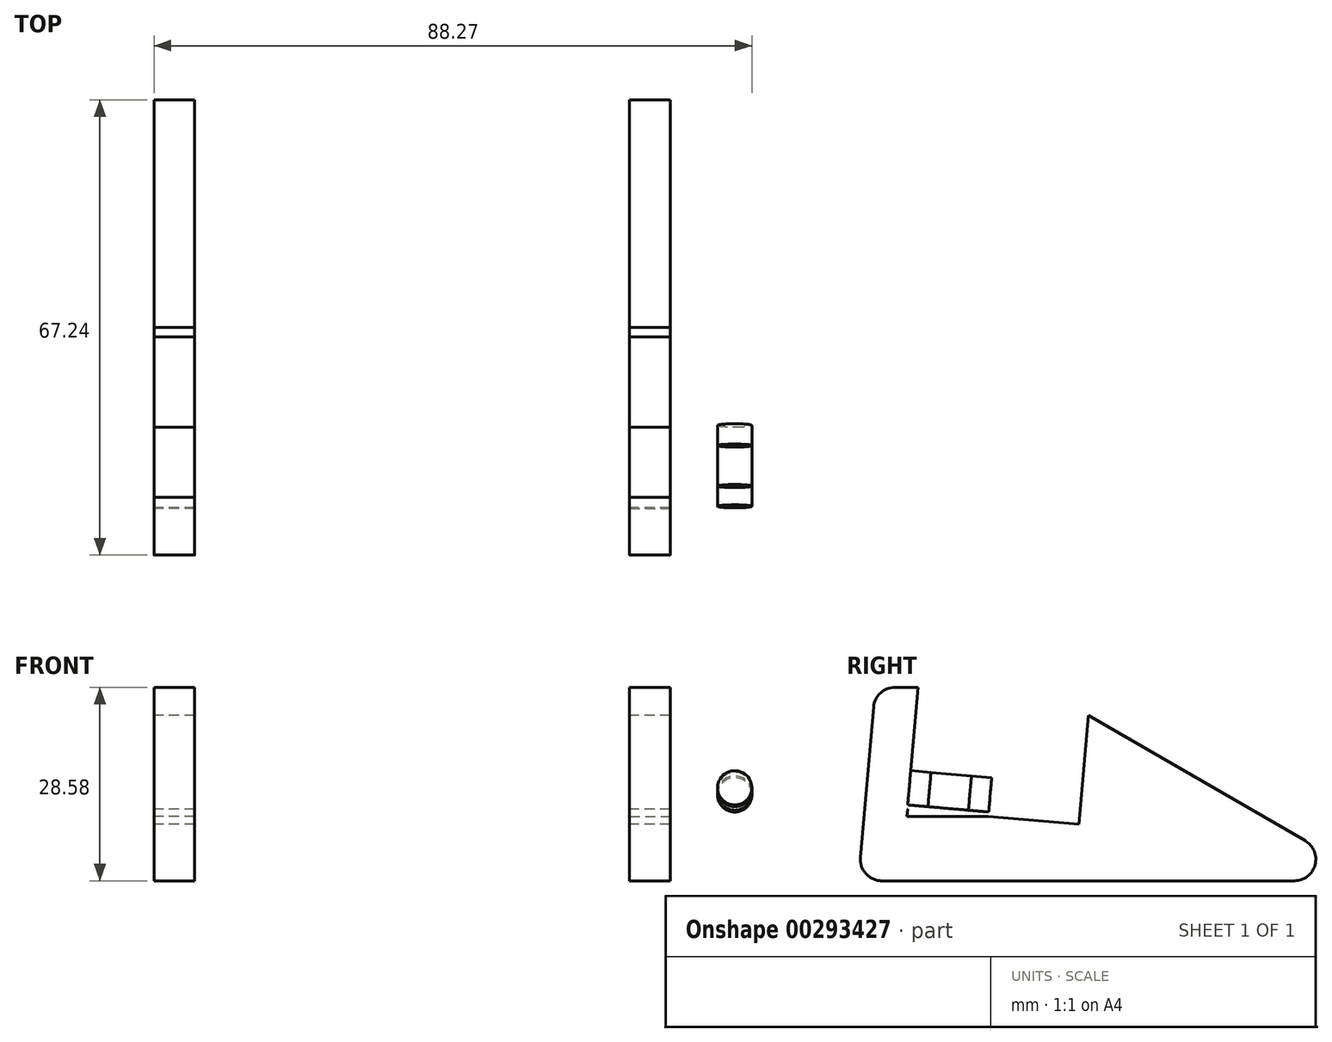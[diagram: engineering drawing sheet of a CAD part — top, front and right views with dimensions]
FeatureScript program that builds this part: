
annotation { "Feature Type Name" : "Feature", "Feature Type Description" : "" }
export const myFeature = defineFeature(function(context is Context, id is Id, definition is map)
    precondition{}
    {
        {
            var Q0;
            Q0=qCreatedBy(makeId("Right.planeOp"),FACE);
            cPlane(context, id + "F0", {"entities" : qUnion([Q0]), "cplaneType" : CPlaneType.OFFSET, "offset" : 38.1 * mm, "oppositeDirection" : true, "width" : 152.4 * mm, "height" : 152.4 * mm});
        }
        {
            var Q0;
            Q0=qCreatedBy(id+"F0.planeOp",FACE);
            var sketch = newSketch(context, id + "F1", { "sketchPlane" : qUnion([Q0])});
            skLineSegment(sketch, "E0", {"start": v(3.46, 0) * mm, "end": v(64.35, 0) * mm});
            skLineSegment(sketch, "E1", {"start": v(65.94, 5.92) * mm, "end": v(27.44, 28.15) * mm});
            skLineSegment(sketch, "E2", {"start": v(25.86, 28.57) * mm, "end": v(20.85, 28.57) * mm});
            skLineSegment(sketch, "E3", {"start": v(20.85, 28.57) * mm, "end": v(19.18, 9.53) * mm});
            skLineSegment(sketch, "E4", {"start": v(19.18, 9.52) * mm, "end": v(7.18, 9.52) * mm});
            skLineSegment(sketch, "E5", {"start": v(7.18, 9.52) * mm, "end": v(8.85, 28.57) * mm});
            skLineSegment(sketch, "E6", {"start": v(8.85, 28.57) * mm, "end": v(5.4, 28.57) * mm});
            skLineSegment(sketch, "E7", {"start": v(2.25, 25.68) * mm, "end": v(0.3, 3.45) * mm});
            skPoint(sketch, "E8.visualSharp", {"position": v(76.2, 0) * mm});
            skArc(sketch, "E8.filletArc", {"start": v(64.35, 0) * mm, "mid": v(67.42, 2.35) * mm, "end": v(65.94, 5.92) * mm});
            skPoint(sketch, "E9.visualSharp", {"position": v(0, 0) * mm});
            skArc(sketch, "E9.filletArc", {"start": v(0.3, 3.45) * mm, "mid": v(1.12, 1.03) * mm, "end": v(3.46, 0) * mm});
            skPoint(sketch, "E10.visualSharp", {"position": v(2.5, 28.57) * mm});
            skArc(sketch, "E10.filletArc", {"start": v(5.4, 28.57) * mm, "mid": v(3.26, 27.74) * mm, "end": v(2.25, 25.68) * mm});
            skPoint(sketch, "E11.visualSharp", {"position": v(26.7, 28.57) * mm});
            skArc(sketch, "E11.filletArc", {"start": v(27.44, 28.15) * mm, "mid": v(26.68, 28.47) * mm, "end": v(25.86, 28.57) * mm});
            skSolve(sketch);
        }
        {
            var Q0;
            Q0=makeQuery(id+"F1.imprint","IMPRINT",FACE,{"disambiguationData":[TD([[makeQuery(id+"F1.imprint","IMPRINT",EDGE,{"derivedFrom":sQuery(id+"F1.wireOp",EDGE,"E0")}),1.0]])]});
            extrude(context, id + "F2", {"entities" : qUnion([Q0]), "depth" : 6 * mm});
        }
        {
            var Q0;
            Q0=makeQuery(id+"F2.opExtrude","SWEPT_BODY",BODY,{"disambiguationData":[OSD([sQuery(id+"F1.wireOp",EDGE,"E0"),sQuery(id+"F1.wireOp",EDGE,"E1"),sQuery(id+"F1.wireOp",EDGE,"E2"),sQuery(id+"F1.wireOp",EDGE,"E3"),sQuery(id+"F1.wireOp",EDGE,"E4"),sQuery(id+"F1.wireOp",EDGE,"E5"),sQuery(id+"F1.wireOp",EDGE,"E6"),sQuery(id+"F1.wireOp",EDGE,"E7"),sQuery(id+"F1.wireOp",EDGE,"E8.filletArc"),sQuery(id+"F1.wireOp",EDGE,"E9.filletArc"),sQuery(id+"F1.wireOp",EDGE,"E10.filletArc"),sQuery(id+"F1.wireOp",EDGE,"E11.filletArc")])]});
            var Q1;
            Q1=qCreatedBy(makeId("Right.planeOp"),FACE);
            mirror(context, id + "F3", {"entities" : qUnion([Q0]), "mirrorPlane" : qUnion([Q1])});
        }
        {
            var Q0;
            Q0=makeQuery(id+"F2.opExtrude","SWEPT_FACE",FACE,{"disambiguationData":[OSD([sQuery(id+"F1.wireOp",EDGE,"E3")])]});
            var sketch = newSketch(context, id + "F4", { "sketchPlane" : qUnion([Q0])});
            skLineSegment(sketch, "E12.bottom", {"start": v(38.1, 11.16) * mm, "end": v(32.1, 11.16) * mm});
            skLineSegment(sketch, "E12.top", {"start": v(57.15, 214.36) * mm, "end": v(-57.15, 214.36) * mm});
            skLineSegment(sketch, "E12.left", {"start": v(57.15, 11.16) * mm, "end": v(57.15, 214.36) * mm});
            skLineSegment(sketch, "E12.right", {"start": v(-57.15, 11.16) * mm, "end": v(-57.15, 214.36) * mm});
            skPoint(sketch, "E12.middle", {"position": v(0, 112.76) * mm});
            skLineSegment(sketch, "E13", {"start": v(-57.15, 138.16) * mm, "end": v(-25.4, 214.36) * mm});
            skLineSegment(sketch, "E14", {"start": v(25.4, 214.36) * mm, "end": v(57.15, 138.16) * mm});
            skLineSegment(sketch, "E15.top", {"start": v(-57.15, 4.81) * mm, "end": v(-38.1, 4.81) * mm});
            skLineSegment(sketch, "E15.right", {"start": v(-38.1, 11.16) * mm, "end": v(-38.1, 4.81) * mm});
            skLineSegment(sketch, "E16.top", {"start": v(57.15, 4.81) * mm, "end": v(38.1, 4.81) * mm});
            skLineSegment(sketch, "E16.right", {"start": v(38.1, 11.16) * mm, "end": v(38.1, 4.81) * mm});
            skLineSegment(sketch, "E17.top", {"start": v(-32.1, 4.81) * mm, "end": v(32.1, 4.81) * mm});
            skLineSegment(sketch, "E17.left", {"start": v(-32.1, 11.16) * mm, "end": v(-32.1, 4.81) * mm});
            skLineSegment(sketch, "E17.right", {"start": v(32.1, 11.16) * mm, "end": v(32.1, 4.81) * mm});
            skLineSegment(sketch, "E18.trimOffspring", {"start": v(-32.1, 11.16) * mm, "end": v(-38.1, 11.16) * mm});
            skLineSegment(sketch, "E19", {"start": v(-57.15, 11.16) * mm, "end": v(-57.15, 4.81) * mm});
            skLineSegment(sketch, "E20", {"start": v(57.15, 11.16) * mm, "end": v(57.15, 4.81) * mm});
            skSolve(sketch);
        }
        {
            var Q0;
            Q0=makeQuery(id+"F4.imprint","IMPRINT",FACE,{"disambiguationData":[TD([[makeQuery(id+"F4.imprint","IMPRINT",EDGE,{"derivedFrom":sQuery(id+"F4.wireOp",EDGE,"E12.bottom")}),-1.0]])]});
            var Q1;
            Q1=makeQuery(id+"F4.imprint","IMPRINT",FACE,{"disambiguationData":[TD([[makeQuery(id+"F4.imprint","IMPRINT",EDGE,{"derivedFrom":sQuery(id+"F4.wireOp",EDGE,"E18.trimOffspring")}),-1.0]])]});
            extrude(context, id + "F5", {"entities" : qUnion([Q0, Q1]), "depth" : 3 * mm});
        }
        {
            var Q0;
            Q0=makeQuery(id+"F5.opExtrude","SWEPT_EDGE",EDGE,{"disambiguationData":[OSD([sQuery(id+"F4.wireOp",EDGE,"E12.right"),sQuery(id+"F4.wireOp",EDGE,"E13")])]});
            var Q1;
            Q1=makeQuery(id+"F5.opExtrude","SWEPT_EDGE",EDGE,{"disambiguationData":[OSD([sQuery(id+"F4.wireOp",EDGE,"E12.left"),sQuery(id+"F4.wireOp",EDGE,"E14")])]});
            fillet(context, id + "F6", {"entities" : qUnion([Q0, Q1]), "radius" : 203.2 * mm, "tangentPropagation" : true, "allowEdgeOverflow" : false});
        }
        {
            var Q0;
            Q0=makeQuery(id+"F5.opExtrude","SWEPT_EDGE",EDGE,{"disambiguationData":[OSD([sQuery(id+"F4.wireOp",EDGE,"E12.top"),sQuery(id+"F4.wireOp",EDGE,"E13")])]});
            var Q1;
            Q1=makeQuery(id+"F5.opExtrude","SWEPT_EDGE",EDGE,{"disambiguationData":[OSD([sQuery(id+"F4.wireOp",EDGE,"E12.top"),sQuery(id+"F4.wireOp",EDGE,"E14")])]});
            fillet(context, id + "F7", {"entities" : qUnion([Q0, Q1]), "radius" : 38.1 * mm, "tangentPropagation" : true, "allowEdgeOverflow" : false});
        }
        {
            var Q0;
            Q0=makeQuery(id+"F5.opExtrude","SWEPT_EDGE",EDGE,{"disambiguationData":[OSD([sQuery(id+"F4.wireOp",EDGE,"E15.top"),sQuery(id+"F4.wireOp",EDGE,"E19")])]});
            var Q1;
            Q1=makeQuery(id+"F5.opExtrude","SWEPT_EDGE",EDGE,{"disambiguationData":[OSD([sQuery(id+"F4.wireOp",EDGE,"E16.top"),sQuery(id+"F4.wireOp",EDGE,"E20")])]});
            fillet(context, id + "F8", {"entities" : qUnion([Q0, Q1]), "radius" : 15.88 * mm, "tangentPropagation" : true, "allowEdgeOverflow" : false});
        }
        {
            var Q0;
            Q0=makeQuery(id+"F5.opExtrude","CAP_FACE",FACE,{"disambiguationData":[OSD([sQuery(id+"F4.wireOp",EDGE,"E12.bottom"),sQuery(id+"F4.wireOp",EDGE,"E12.top"),sQuery(id+"F4.wireOp",EDGE,"E12.left"),sQuery(id+"F4.wireOp",EDGE,"E12.right"),sQuery(id+"F4.wireOp",EDGE,"E13"),sQuery(id+"F4.wireOp",EDGE,"E14"),sQuery(id+"F4.wireOp",EDGE,"E15.top"),sQuery(id+"F4.wireOp",EDGE,"E15.right"),sQuery(id+"F4.wireOp",EDGE,"E16.top"),sQuery(id+"F4.wireOp",EDGE,"E16.right"),sQuery(id+"F4.wireOp",EDGE,"E17.top"),sQuery(id+"F4.wireOp",EDGE,"E17.left"),sQuery(id+"F4.wireOp",EDGE,"E17.right"),sQuery(id+"F4.wireOp",EDGE,"E18.trimOffspring"),sQuery(id+"F4.wireOp",EDGE,"E19"),sQuery(id+"F4.wireOp",EDGE,"E20")])],"isStart":false});
            extrude(context, id + "F9", {"entities" : qUnion([Q0]), "depth" : 6 * mm});
        }
        {
            var Q0;
            Q0=makeQuery(id+"F9.opExtrude","CAP_FACE",FACE,{"disambiguationData":[OSD([sQuery(id+"F4.wireOp",EDGE,"E12.bottom"),sQuery(id+"F4.wireOp",EDGE,"E12.top"),sQuery(id+"F4.wireOp",EDGE,"E12.left"),sQuery(id+"F4.wireOp",EDGE,"E12.right"),sQuery(id+"F4.wireOp",EDGE,"E13"),sQuery(id+"F4.wireOp",EDGE,"E14"),sQuery(id+"F4.wireOp",EDGE,"E15.top"),sQuery(id+"F4.wireOp",EDGE,"E15.right"),sQuery(id+"F4.wireOp",EDGE,"E16.top"),sQuery(id+"F4.wireOp",EDGE,"E16.right"),sQuery(id+"F4.wireOp",EDGE,"E17.top"),sQuery(id+"F4.wireOp",EDGE,"E17.left"),sQuery(id+"F4.wireOp",EDGE,"E17.right"),sQuery(id+"F4.wireOp",EDGE,"E18.trimOffspring"),sQuery(id+"F4.wireOp",EDGE,"E19"),sQuery(id+"F4.wireOp",EDGE,"E20")])],"isStart":false});
            extrude(context, id + "F10", {"entities" : qUnion([Q0]), "depth" : 3 * mm});
        }
        {
            var Q0;
            Q0=makeQuery(id+"F10.opExtrude","CAP_FACE",FACE,{"disambiguationData":[OSD([sQuery(id+"F4.wireOp",EDGE,"E12.bottom"),sQuery(id+"F4.wireOp",EDGE,"E12.top"),sQuery(id+"F4.wireOp",EDGE,"E12.left"),sQuery(id+"F4.wireOp",EDGE,"E12.right"),sQuery(id+"F4.wireOp",EDGE,"E13"),sQuery(id+"F4.wireOp",EDGE,"E14"),sQuery(id+"F4.wireOp",EDGE,"E15.top"),sQuery(id+"F4.wireOp",EDGE,"E15.right"),sQuery(id+"F4.wireOp",EDGE,"E16.top"),sQuery(id+"F4.wireOp",EDGE,"E16.right"),sQuery(id+"F4.wireOp",EDGE,"E17.top"),sQuery(id+"F4.wireOp",EDGE,"E17.left"),sQuery(id+"F4.wireOp",EDGE,"E17.right"),sQuery(id+"F4.wireOp",EDGE,"E18.trimOffspring"),sQuery(id+"F4.wireOp",EDGE,"E19"),sQuery(id+"F4.wireOp",EDGE,"E20")])],"isStart":false});
            var sketch = newSketch(context, id + "F11", { "sketchPlane" : qUnion([Q0])});
            skCircle(sketch, "E21", {"center": v(-47.62, 14.34) * mm, "radius": 2.54 * mm});
            skLineSegment(sketch, "E22", {"start": v(0, 0) * mm, "end": v(0, 36.43) * mm, "construction": true});
            skPoint(sketch, "E22.endSnap0", {"position": v(0, 4.81) * mm});
            skLineSegment(sketch, "E23", {"start": v(-47.62, 14.34) * mm, "end": v(0, 14.34) * mm, "construction": true});
            skLineSegment(sketch, "E24.MirrorCS", {"start": v(47.62, 14.34) * mm, "end": v(0, 14.34) * mm, "construction": true});
            skCircle(sketch, "E25.MirrorC", {"center": v(47.62, 14.34) * mm, "radius": 2.54 * mm});
            skCircle(sketch, "E26", {"center": v(0, 208.01) * mm, "radius": 2.54 * mm});
            skSolve(sketch);
        }
        {
            var Q0;
            Q0=makeQuery(id+"F11.imprint","IMPRINT",FACE,{"disambiguationData":[TD([[makeQuery(id+"F11.imprint","IMPRINT",EDGE,{"derivedFrom":sQuery(id+"F11.wireOp",EDGE,"E21")}),1.0]])]});
            var Q1;
            Q1=makeQuery(id+"F11.imprint","IMPRINT",FACE,{"disambiguationData":[TD([[makeQuery(id+"F11.imprint","IMPRINT",EDGE,{"derivedFrom":sQuery(id+"F11.wireOp",EDGE,"E25.MirrorC")}),-1.0]])]});
            var Q2;
            Q2=makeQuery(id+"F11.imprint","IMPRINT",FACE,{"disambiguationData":[TD([[makeQuery(id+"F11.imprint","IMPRINT",EDGE,{"derivedFrom":sQuery(id+"F11.wireOp",EDGE,"E26")}),1.0]])]});
            extrude(context, id + "F12", {"entities" : qUnion([Q0, Q1, Q2]), "operationType" : NewBodyOperationType.REMOVE, "oppositeDirection" : true, "depth" : 25.4 * mm});
        }
    });
